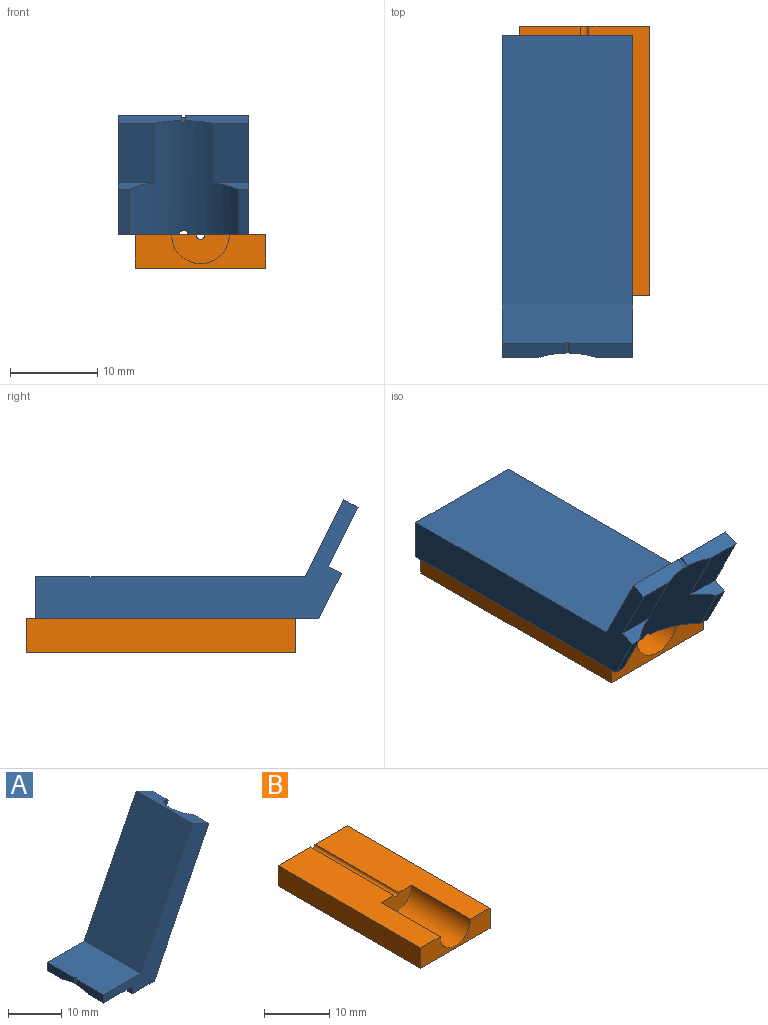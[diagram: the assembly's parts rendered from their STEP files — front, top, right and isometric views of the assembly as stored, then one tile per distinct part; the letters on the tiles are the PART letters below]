
ASSEMBLY  parts=2 mates=1
PART A: 20 faces, bbox 28x15x31.2 mm
  f0: plane 29x14.49mm, normal (0.89,0,-0.45), area 181mm2, adj f8,f9,f10,f15,f17,f18,f19
  f1: plane 29x14.49mm, normal (0.89,0,-0.45), area 181mm2, adj f5,f10,f13,f15,f17,f18,f19
  f2: plane 7.24x1.85mm, normal (-1,0,0), area 12.1mm2, adj f4,f9,f12,f15,f16
  f3: plane 7.62x4.09mm, normal (0,0,-1), area 31.1mm2, adj f7,f13,f14,f15
  f4: plane 7.62x4.09mm, normal (0,0,-1), area 31.1mm2, adj f2,f6,f9,f15
  f5: plane 5.84x1.25mm, normal (0,0,-1), area 7.3mm2, adj f1,f13,f14,f15
  f6: plane 4.09x1.7mm, normal (-1,0,0), area 4.2mm2, adj f4,f8,f9,f15
  f7: plane 7.24x1.85mm, normal (-1,0,0), area 12.1mm2, adj f3,f12,f13,f15,f16
  f8: plane 5.84x1.25mm, normal (0,0,-1), area 7.3mm2, adj f0,f6,f9,f15
  f9: plane 31.16x27.96mm, normal (0,-1,0), area 181.2mm2, adj f0,f2,f4,f6,f8,f10,f11,f12
  f10: plane 14.99x4.32mm, normal (0.45,0,0.89), area 55.2mm2, adj f0,f1,f9,f11,f13,f18
  f11: plane 27.6x14.99mm, normal (-0.89,0,0.45), area 462.5mm2, adj f9,f10,f12,f13
  f12: plane 14.99x9.84mm, normal (0,0,1), area 147.4mm2, adj f2,f7,f9,f11,f13,f16
  f13: plane 31.16x27.96mm, normal (0,1,0), area 181.2mm2, adj f1,f3,f5,f7,f10,f11,f12,f14
  f14: plane 4.09x1.7mm, normal (-1,0,0), area 4.2mm2, adj f3,f5,f13,f15
  f15: cylinder r=9.53mm len=14.62mm, axis (-1,0,0), area 142.6mm2, adj f0,f1,f2,f3,f4,f5,f6,f7
  f16: cylinder r=0.25mm len=1.23mm, axis (0,0,1), area 1mm2, adj f2,f7,f12,f15
  f17: cylinder r=0.51mm len=15.7mm, axis (0.45,0,0.89), area 27.5mm2, adj f0,f1,f15,f19
  f18: cylinder r=3.3mm len=12.9mm, axis (0.45,0,0.89), area 132.5mm2, adj f0,f1,f10,f19
  f19: plane 6.6x2.95mm, normal (0.45,0,0.89), area 16.7mm2, adj f0,f1,f17,f18
PART B: 10 faces, bbox 15x30.9x3.8 mm
  f0: plane 30.86x6.99mm, normal (0,0,1), area 179.9mm2, adj f2,f5,f6,f7,f8,f9
  f1: plane 30.86x6.99mm, normal (0,0,1), area 179.9mm2, adj f4,f5,f6,f7,f8,f9
  f2: plane 30.86x3.81mm, normal (-1,0,0), area 117.6mm2, adj f0,f3,f5,f6
  f3: plane 30.86x14.99mm, normal (0,0,-1), area 462.5mm2, adj f2,f4,f5,f6
  f4: plane 30.86x3.81mm, normal (1,0,0), area 117.6mm2, adj f1,f3,f5,f6
  f5: plane 14.99x3.81mm, normal (0,-1,0), area 40mm2, adj f0,f1,f2,f3,f4,f7
  f6: plane 14.99x3.81mm, normal (0,1,0), area 56.7mm2, adj f0,f1,f2,f3,f4,f9
  f7: cylinder r=3.3mm len=12.78mm, axis (0,-1,0), area 132.5mm2, adj f0,f1,f5,f8
  f8: plane 6.6x3.3mm, normal (0,-1,0), area 16.7mm2, adj f0,f1,f7,f9
  f9: cylinder r=0.51mm len=18.09mm, axis (0,-1,0), area 28.9mm2, adj f0,f1,f6,f8
PLACE A rot(axis=(-0.47,0.47,0.75),106.1deg) t=(3.22,-9.55,17.68)mm
PLACE B t=(9.16,31.74,2.62)mm
MATE planar A.f0 <-> B.f0  axis (0,0,-1) through (15.2,13.27,2.23)mm
